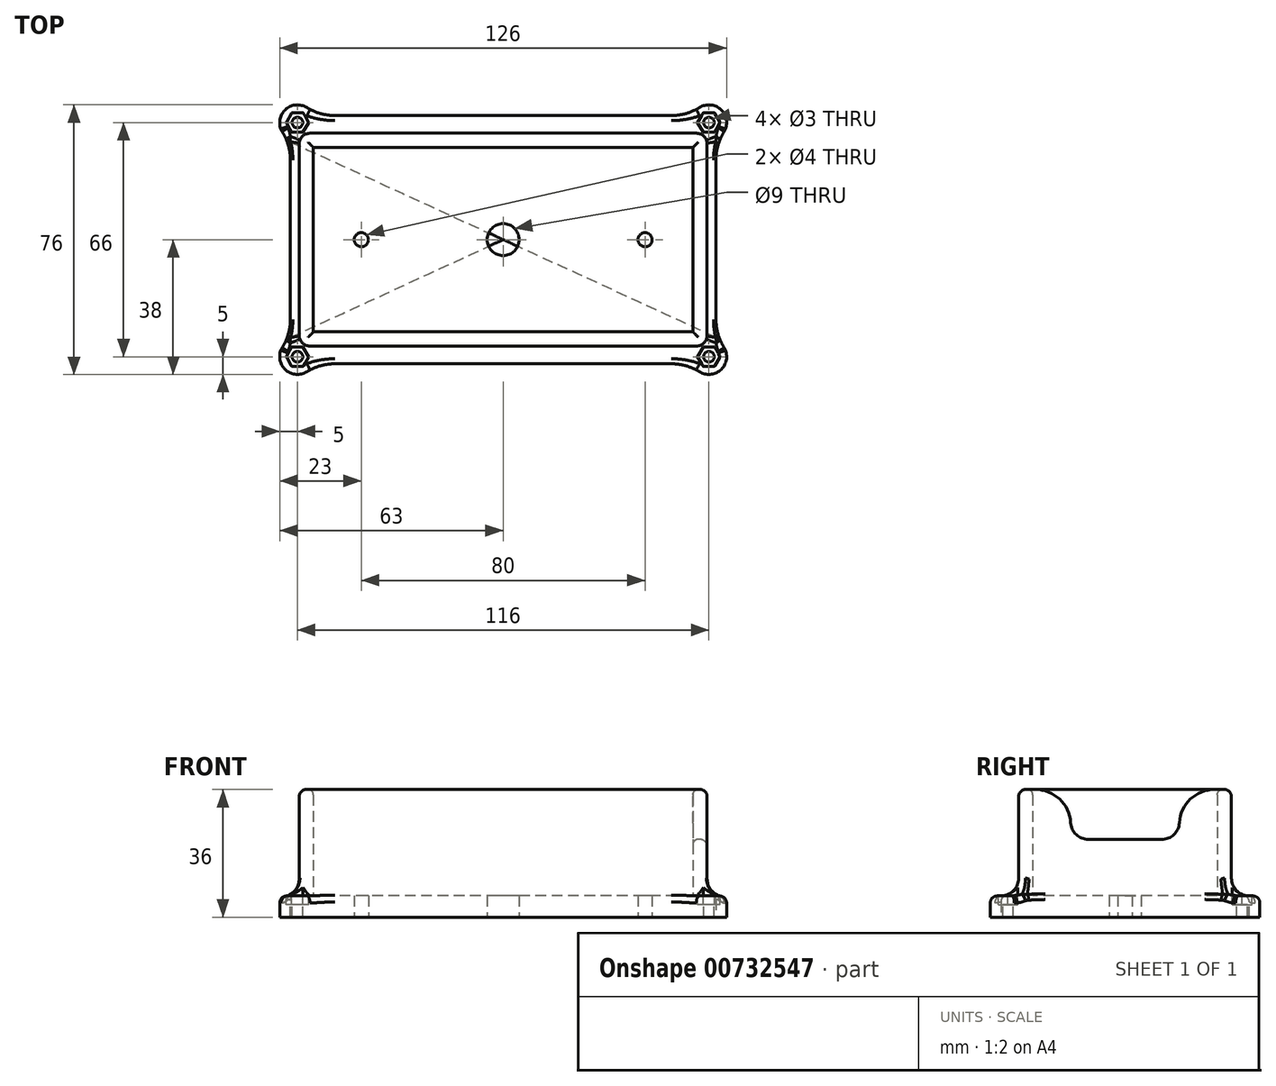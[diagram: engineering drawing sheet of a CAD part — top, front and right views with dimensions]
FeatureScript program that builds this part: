
annotation { "Feature Type Name" : "Feature", "Feature Type Description" : "" }
export const myFeature = defineFeature(function(context is Context, id is Id, definition is map)
    precondition{}
    {
        {
            var Q0;
            Q0=qCreatedBy(makeId("Top.planeOp"),FACE);
            var sketch = newSketch(context, id + "F0", { "sketchPlane" : qUnion([Q0])});
            skLineSegment(sketch, "E0.bottom", {"start": v(53.42, 35) * mm, "end": v(-53.42, 35) * mm});
            skLineSegment(sketch, "E0.top", {"start": v(53.42, -35) * mm, "end": v(-53.42, -35) * mm});
            skLineSegment(sketch, "E0.left", {"start": v(60, 28.42) * mm, "end": v(60, -28.42) * mm});
            skLineSegment(sketch, "E0.right", {"start": v(-60, 28.42) * mm, "end": v(-60, -28.42) * mm});
            skPoint(sketch, "E0.middle", {"position": v(0, 0) * mm});
            skLineSegment(sketch, "E1.bottom", {"start": v(58, -33) * mm, "end": v(-58, -33) * mm, "construction": true});
            skLineSegment(sketch, "E1.top", {"start": v(58, 33) * mm, "end": v(-58, 33) * mm, "construction": true});
            skLineSegment(sketch, "E1.left", {"start": v(58, 33) * mm, "end": v(58, -33) * mm, "construction": true});
            skLineSegment(sketch, "E1.right", {"start": v(-58, 33) * mm, "end": v(-58, -33) * mm, "construction": true});
            skArc(sketch, "E2", {"start": v(-53.42, 35) * mm, "mid": v(-61.54, 36.54) * mm, "end": v(-60, 28.42) * mm});
            skArc(sketch, "E3", {"start": v(-60, -28.42) * mm, "mid": v(-61.54, -36.54) * mm, "end": v(-53.42, -35) * mm});
            skArc(sketch, "E4", {"start": v(60, 28.42) * mm, "mid": v(61.54, 36.54) * mm, "end": v(53.42, 35) * mm});
            skArc(sketch, "E5", {"start": v(53.42, -35) * mm, "mid": v(61.54, -36.54) * mm, "end": v(60, -28.42) * mm});
            skPoint(sketch, "E6.orphan", {"position": v(-60, 35) * mm});
            skPoint(sketch, "E7.orphan", {"position": v(60, 35) * mm});
            skPoint(sketch, "E8.orphan", {"position": v(60, -35) * mm});
            skPoint(sketch, "E9.orphan", {"position": v(-60, -35) * mm});
            skSolve(sketch);
        }
        {
            var Q0;
            Q0=qSketchRegion(id+"F0",true);
            extrude(context, id + "F1", {"entities" : qUnion([Q0]), "depth" : 6 * mm, "offsetDistance" : 25 * mm});
        }
        {
            var Q0;
            Q0=makeQuery(id+"F1.opExtrude","SWEPT_EDGE",EDGE,{"disambiguationData":[OSD([sQuery(id+"F0.wireOp",EDGE,"E0.bottom"),sQuery(id+"F0.wireOp",EDGE,"E2")])]});
            var Q1;
            Q1=makeQuery(id+"F1.opExtrude","SWEPT_EDGE",EDGE,{"disambiguationData":[OSD([sQuery(id+"F0.wireOp",EDGE,"E0.bottom"),sQuery(id+"F0.wireOp",EDGE,"E4")])]});
            var Q2;
            Q2=makeQuery(id+"F1.opExtrude","SWEPT_EDGE",EDGE,{"disambiguationData":[OSD([sQuery(id+"F0.wireOp",EDGE,"E0.left"),sQuery(id+"F0.wireOp",EDGE,"E5")])]});
            var Q3;
            Q3=makeQuery(id+"F1.opExtrude","SWEPT_EDGE",EDGE,{"disambiguationData":[OSD([sQuery(id+"F0.wireOp",EDGE,"E0.left"),sQuery(id+"F0.wireOp",EDGE,"E4")])]});
            var Q4;
            Q4=makeQuery(id+"F1.opExtrude","SWEPT_EDGE",EDGE,{"disambiguationData":[OSD([sQuery(id+"F0.wireOp",EDGE,"E0.top"),sQuery(id+"F0.wireOp",EDGE,"E5")])]});
            var Q5;
            Q5=makeQuery(id+"F1.opExtrude","SWEPT_EDGE",EDGE,{"disambiguationData":[OSD([sQuery(id+"F0.wireOp",EDGE,"E0.top"),sQuery(id+"F0.wireOp",EDGE,"E3")])]});
            var Q6;
            Q6=makeQuery(id+"F1.opExtrude","SWEPT_EDGE",EDGE,{"disambiguationData":[OSD([sQuery(id+"F0.wireOp",EDGE,"E0.right"),sQuery(id+"F0.wireOp",EDGE,"E3")])]});
            var Q7;
            Q7=makeQuery(id+"F1.opExtrude","SWEPT_EDGE",EDGE,{"disambiguationData":[OSD([sQuery(id+"F0.wireOp",EDGE,"E0.right"),sQuery(id+"F0.wireOp",EDGE,"E2")])]});
            fillet(context, id + "F2", {"entities" : qUnion([Q0, Q1, Q2, Q3, Q4, Q5, Q6, Q7]), "radius" : 15 * mm, "tangentPropagation" : true, "allowEdgeOverflow" : false});
        }
        {
            var Q0;
            Q0=makeQuery(id+"F1.opExtrude","CAP_FACE",FACE,{"disambiguationData":[OSD([sQuery(id+"F0.wireOp",EDGE,"E0.bottom"),sQuery(id+"F0.wireOp",EDGE,"E0.top"),sQuery(id+"F0.wireOp",EDGE,"E0.left"),sQuery(id+"F0.wireOp",EDGE,"E0.right"),sQuery(id+"F0.wireOp",EDGE,"E2"),sQuery(id+"F0.wireOp",EDGE,"E3"),sQuery(id+"F0.wireOp",EDGE,"E4"),sQuery(id+"F0.wireOp",EDGE,"E5")])],"isStart":false});
            var sketch = newSketch(context, id + "F3", { "sketchPlane" : qUnion([Q0])});
            skLineSegment(sketch, "E10.bottom", {"start": v(57.5, 30) * mm, "end": v(-57.5, 30) * mm});
            skLineSegment(sketch, "E10.top", {"start": v(57.5, -30) * mm, "end": v(-57.5, -30) * mm});
            skLineSegment(sketch, "E10.left", {"start": v(57.5, 30) * mm, "end": v(57.5, -30) * mm});
            skLineSegment(sketch, "E10.right", {"start": v(-57.5, 30) * mm, "end": v(-57.5, -30) * mm});
            skPoint(sketch, "E10.middle", {"position": v(0, 0) * mm});
            skLineSegment(sketch, "E11.bottom", {"start": v(53.5, 26) * mm, "end": v(-53.5, 26) * mm});
            skLineSegment(sketch, "E11.top", {"start": v(53.5, -26) * mm, "end": v(-53.5, -26) * mm});
            skLineSegment(sketch, "E11.left", {"start": v(53.5, 26) * mm, "end": v(53.5, -26) * mm});
            skLineSegment(sketch, "E11.right", {"start": v(-53.5, 26) * mm, "end": v(-53.5, -26) * mm});
            skSolve(sketch);
        }
        {
            var Q0;
            Q0=qSketchRegion(id+"F3",true);
            extrude(context, id + "F4", {"entities" : qUnion([Q0]), "operationType" : NewBodyOperationType.ADD, "depth" : 30 * mm, "offsetDistance" : 25 * mm});
        }
        {
            var Q0;
            Q0=makeQuery(id+"F4.opExtrude","SWEPT_EDGE",EDGE,{"disambiguationData":[OSD([sQuery(id+"F3.wireOp",EDGE,"E10.top"),sQuery(id+"F3.wireOp",EDGE,"E10.right")])]});
            var Q1;
            Q1=makeQuery(id+"F4.opExtrude","SWEPT_EDGE",EDGE,{"disambiguationData":[OSD([sQuery(id+"F3.wireOp",EDGE,"E10.top"),sQuery(id+"F3.wireOp",EDGE,"E10.left")])]});
            var Q2;
            Q2=makeQuery(id+"F4.opExtrude","SWEPT_EDGE",EDGE,{"disambiguationData":[OSD([sQuery(id+"F3.wireOp",EDGE,"E10.bottom"),sQuery(id+"F3.wireOp",EDGE,"E10.left")])]});
            var Q3;
            Q3=makeQuery(id+"F4.opExtrude","SWEPT_EDGE",EDGE,{"disambiguationData":[OSD([sQuery(id+"F3.wireOp",EDGE,"E10.bottom"),sQuery(id+"F3.wireOp",EDGE,"E10.right")])]});
            fillet(context, id + "F5", {"entities" : qUnion([Q0, Q1, Q2, Q3]), "radius" : 3 * mm, "allowEdgeOverflow" : false});
        }
        {
            var Q0;
            Q0=makeQuery(id+"F4.opExtrude","CAP_EDGE",EDGE,{"disambiguationData":[OSD([sQuery(id+"F3.wireOp",EDGE,"E10.bottom")])],"isStart":true});
            fillet(context, id + "F6", {"entities" : qUnion([Q0]), "radius" : 5 * mm, "tangentPropagation" : true, "allowEdgeOverflow" : false});
        }
        {
            var Q0;
            Q0=makeQuery(id+"F6.opFillet","BLEND_EDGE",EDGE,{"blendedFrom":[makeQuery(id+"F4.opExtrude","CAP_EDGE",EDGE,{"disambiguationData":[OSD([sQuery(id+"F3.wireOp",EDGE,"E10.bottom")])],"isStart":true}),makeQuery(id+"F1.opExtrude","SWEPT_FACE",FACE,{"disambiguationData":[OSD([sQuery(id+"F0.wireOp",EDGE,"E0.bottom")])]})],"blendedInto":[makeQuery(id+"F1.opExtrude","SWEPT_FACE",FACE,{"disambiguationData":[OSD([sQuery(id+"F0.wireOp",EDGE,"E0.bottom")])]})]});
            fillet(context, id + "F7", {"entities" : qUnion([Q0]), "radius" : 2 * mm, "tangentPropagation" : true, "allowEdgeOverflow" : false});
        }
        {
            var Q0;
            Q0=makeQuery(id+"F4.opExtrude","SWEPT_FACE",FACE,{"disambiguationData":[OSD([sQuery(id+"F3.wireOp",EDGE,"E10.left")])]});
            var sketch = newSketch(context, id + "F8", { "sketchPlane" : qUnion([Q0])});
            skLineSegment(sketch, "E12.bottom", {"start": v(15.3, 21.93) * mm, "end": v(-15.3, 21.93) * mm});
            skLineSegment(sketch, "E12.top", {"start": v(15.3, 50.07) * mm, "end": v(-15.3, 50.07) * mm});
            skLineSegment(sketch, "E12.left", {"start": v(15.3, 21.93) * mm, "end": v(15.3, 50.07) * mm});
            skLineSegment(sketch, "E12.right", {"start": v(-15.3, 21.93) * mm, "end": v(-15.3, 50.07) * mm});
            skPoint(sketch, "E12.middle", {"position": v(0, 36) * mm});
            skSolve(sketch);
        }
        {
            var Q0;
            Q0 = qSketchRegion(id + "F8", true);
            extrude(context, id + "F9", {"entities" : qUnion([Q0]), "operationType" : NewBodyOperationType.REMOVE, "oppositeDirection" : true, "depth" : 25 * mm, "offsetDistance" : 25 * mm});
        }
        {
            var Q0;
            Q0=makeQuery(id+"F9.boolean.opBoolean","INTERSECT",EDGE,{"derivedFrom":[makeQuery(id+"F4.opExtrude","CAP_FACE",FACE,{"disambiguationData":[OSD([sQuery(id+"F3.wireOp",EDGE,"E10.bottom"),sQuery(id+"F3.wireOp",EDGE,"E10.top"),sQuery(id+"F3.wireOp",EDGE,"E10.left"),sQuery(id+"F3.wireOp",EDGE,"E10.right"),sQuery(id+"F3.wireOp",EDGE,"E11.bottom"),sQuery(id+"F3.wireOp",EDGE,"E11.top"),sQuery(id+"F3.wireOp",EDGE,"E11.left"),sQuery(id+"F3.wireOp",EDGE,"E11.right")])],"isStart":false}),makeQuery(id+"F9.opExtrude","SWEPT_FACE",FACE,{"disambiguationData":[OSD([sQuery(id+"F8.wireOp",EDGE,"E12.left")])]})]});
            var Q1;
            Q1=makeQuery(id+"F9.boolean.opBoolean","INTERSECT",EDGE,{"derivedFrom":[makeQuery(id+"F4.opExtrude","CAP_FACE",FACE,{"disambiguationData":[OSD([sQuery(id+"F3.wireOp",EDGE,"E10.bottom"),sQuery(id+"F3.wireOp",EDGE,"E10.top"),sQuery(id+"F3.wireOp",EDGE,"E10.left"),sQuery(id+"F3.wireOp",EDGE,"E10.right"),sQuery(id+"F3.wireOp",EDGE,"E11.bottom"),sQuery(id+"F3.wireOp",EDGE,"E11.top"),sQuery(id+"F3.wireOp",EDGE,"E11.left"),sQuery(id+"F3.wireOp",EDGE,"E11.right")])],"isStart":false}),makeQuery(id+"F9.opExtrude","SWEPT_FACE",FACE,{"disambiguationData":[OSD([sQuery(id+"F8.wireOp",EDGE,"E12.right")])]})]});
            fillet(context, id + "F10", {"entities" : qUnion([Q0, Q1]), "radius" : 10 * mm, "tangentPropagation" : true, "allowEdgeOverflow" : false});
        }
        {
            var Q0;
            Q0=makeQuery(id+"F9.boolean.opBoolean","COPY",EDGE,{"derivedFrom":makeQuery(id+"F9.opExtrude","SWEPT_EDGE",EDGE,{"disambiguationData":[OSD([sQuery(id+"F8.wireOp",EDGE,"E12.bottom"),sQuery(id+"F8.wireOp",EDGE,"E12.left")])]})});
            var Q1;
            Q1=makeQuery(id+"F9.boolean.opBoolean","COPY",EDGE,{"derivedFrom":makeQuery(id+"F9.opExtrude","SWEPT_EDGE",EDGE,{"disambiguationData":[OSD([sQuery(id+"F8.wireOp",EDGE,"E12.bottom"),sQuery(id+"F8.wireOp",EDGE,"E12.right")])]})});
            fillet(context, id + "F11", {"entities" : qUnion([Q0, Q1]), "radius" : 5 * mm, "tangentPropagation" : true, "allowEdgeOverflow" : false});
        }
        {
            var Q0;
            Q0=makeQuery(id+"FcA09zrrW4XeXJK_1.boolean.opBoolean","COPY",EDGE,{"derivedFrom":makeQuery(id+"FcA09zrrW4XeXJK_1.opExtrude","CAP_EDGE",EDGE,{"disambiguationData":[OSD([sQuery(id+"Fv4TZC5OFzZsvTr_1.wireOp",EDGE,"FDxE1tWj-xLRE-T8vv-3hwI-uIhzQXojzkdN")])],"isStart":true})});
            var Q1;
            Q1=makeQuery(id+"F4.opExtrude","CAP_EDGE",EDGE,{"disambiguationData":[OSD([sQuery(id+"F3.wireOp",EDGE,"E10.top")])],"isStart":false});
            fillet(context, id + "F12", {"entities" : qUnion([Q0, Q1]), "radius" : 2 * mm, "tangentPropagation" : true, "allowEdgeOverflow" : false});
        }
        {
            var Q0;
            Q0=makeQuery(id+"F4.opExtrude","CAP_EDGE",EDGE,{"disambiguationData":[OSD([sQuery(id+"F3.wireOp",EDGE,"E11.right")])],"isStart":false});
            var Q1;
            Q1=makeQuery(id+"F4.opExtrude","CAP_EDGE",EDGE,{"disambiguationData":[OSD([sQuery(id+"F3.wireOp",EDGE,"E11.bottom")])],"isStart":false});
            var Q2;
            Q2=makeQuery(id+"F4.opExtrude","CAP_EDGE",EDGE,{"disambiguationData":[OSD([sQuery(id+"F3.wireOp",EDGE,"E11.left")])],"isStart":false});
            var Q3;
            Q3=makeQuery(id+"F4.opExtrude","CAP_EDGE",EDGE,{"disambiguationData":[OSD([sQuery(id+"F3.wireOp",EDGE,"E11.top")])],"isStart":false});
            fillet(context, id + "F13", {"entities" : qUnion([Q0, Q1, Q2, Q3]), "radius" : 1.5 * mm, "tangentPropagation" : true, "allowEdgeOverflow" : false});
        }
        {
            var Q0;
            Q0=makeQuery(id+"F4.boolean.opBoolean","SPLIT",FACE,{"disambiguationData":[TD([makeQuery(id+"F4.opExtrude","SWEPT_FACE",FACE,{"disambiguationData":[OSD([sQuery(id+"F3.wireOp",EDGE,"E11.bottom")])]})])],"derivedFrom":makeQuery(id+"F1.opExtrude","CAP_FACE",FACE,{"disambiguationData":[OSD([sQuery(id+"F0.wireOp",EDGE,"E0.bottom"),sQuery(id+"F0.wireOp",EDGE,"E0.top"),sQuery(id+"F0.wireOp",EDGE,"E0.left"),sQuery(id+"F0.wireOp",EDGE,"E0.right"),sQuery(id+"F0.wireOp",EDGE,"E2"),sQuery(id+"F0.wireOp",EDGE,"E3"),sQuery(id+"F0.wireOp",EDGE,"E4"),sQuery(id+"F0.wireOp",EDGE,"E5")])],"isStart":false})});
            var sketch = newSketch(context, id + "F14", { "sketchPlane" : qUnion([Q0])});
            skLineSegment(sketch, "E13.bottom", {"start": v(58, 33) * mm, "end": v(-58, 33) * mm, "construction": true});
            skLineSegment(sketch, "E13.top", {"start": v(58, -33) * mm, "end": v(-58, -33) * mm, "construction": true});
            skLineSegment(sketch, "E13.left", {"start": v(58, 33) * mm, "end": v(58, -33) * mm, "construction": true});
            skLineSegment(sketch, "E13.right", {"start": v(-58, 33) * mm, "end": v(-58, -33) * mm, "construction": true});
            skPoint(sketch, "E13.middle", {"position": v(0, 0) * mm});
            skCircle(sketch, "E14.cCircle", {"center": v(-58, 33) * mm, "radius": 2.75 * mm, "construction": true});
            skLineSegment(sketch, "E14.0", {"start": v(-56.41, 30.25) * mm, "end": v(-59.59, 30.25) * mm});
            skLineSegment(sketch, "E14.1", {"start": v(-59.59, 30.25) * mm, "end": v(-61.18, 33) * mm});
            skLineSegment(sketch, "E14.2", {"start": v(-61.18, 33) * mm, "end": v(-59.59, 35.75) * mm});
            skLineSegment(sketch, "E14.3", {"start": v(-59.59, 35.75) * mm, "end": v(-56.41, 35.75) * mm});
            skLineSegment(sketch, "E14.4", {"start": v(-56.41, 35.75) * mm, "end": v(-54.82, 33) * mm});
            skLineSegment(sketch, "E14.5", {"start": v(-54.82, 33) * mm, "end": v(-56.41, 30.25) * mm});
            skPoint(sketch, "E14.0.midPoint", {"position": v(-58, 30.25) * mm});
            skCircle(sketch, "E15.cCircle", {"center": v(58, 33) * mm, "radius": 2.75 * mm, "construction": true});
            skLineSegment(sketch, "E15.0", {"start": v(54.82, 33) * mm, "end": v(56.41, 35.75) * mm});
            skLineSegment(sketch, "E15.1", {"start": v(56.41, 35.75) * mm, "end": v(59.59, 35.75) * mm});
            skLineSegment(sketch, "E15.2", {"start": v(59.59, 35.75) * mm, "end": v(61.18, 33) * mm});
            skLineSegment(sketch, "E15.3", {"start": v(61.18, 33) * mm, "end": v(59.59, 30.25) * mm});
            skLineSegment(sketch, "E15.4", {"start": v(59.59, 30.25) * mm, "end": v(56.41, 30.25) * mm});
            skLineSegment(sketch, "E15.5", {"start": v(56.41, 30.25) * mm, "end": v(54.82, 33) * mm});
            skPoint(sketch, "E15.0.midPoint", {"position": v(55.62, 34.38) * mm});
            skCircle(sketch, "E16.cCircle", {"center": v(58, -33) * mm, "radius": 2.75 * mm, "construction": true});
            skPoint(sketch, "E16.cCircle.perimeterSnap0", {"position": v(55.62, 31.62) * mm});
            skLineSegment(sketch, "E16.0", {"start": v(56.41, -35.75) * mm, "end": v(54.82, -33) * mm});
            skLineSegment(sketch, "E16.1", {"start": v(54.82, -33) * mm, "end": v(56.41, -30.25) * mm});
            skLineSegment(sketch, "E16.2", {"start": v(56.41, -30.25) * mm, "end": v(59.59, -30.25) * mm});
            skLineSegment(sketch, "E16.3", {"start": v(59.59, -30.25) * mm, "end": v(61.18, -33) * mm});
            skLineSegment(sketch, "E16.4", {"start": v(61.18, -33) * mm, "end": v(59.59, -35.75) * mm});
            skLineSegment(sketch, "E16.5", {"start": v(59.59, -35.75) * mm, "end": v(56.41, -35.75) * mm});
            skPoint(sketch, "E16.0.midPoint", {"position": v(55.62, -34.38) * mm});
            skPoint(sketch, "E16.0.midPoint.positionSnap0", {"position": v(55.62, 31.63) * mm});
            skCircle(sketch, "E17.cCircle", {"center": v(-58, -33) * mm, "radius": 2.75 * mm, "construction": true});
            skLineSegment(sketch, "E17.0", {"start": v(-59.59, -35.75) * mm, "end": v(-61.18, -33) * mm});
            skLineSegment(sketch, "E17.1", {"start": v(-61.18, -33) * mm, "end": v(-59.59, -30.25) * mm});
            skLineSegment(sketch, "E17.2", {"start": v(-59.59, -30.25) * mm, "end": v(-56.41, -30.25) * mm});
            skLineSegment(sketch, "E17.3", {"start": v(-56.41, -30.25) * mm, "end": v(-54.82, -33) * mm});
            skLineSegment(sketch, "E17.4", {"start": v(-54.82, -33) * mm, "end": v(-56.41, -35.75) * mm});
            skLineSegment(sketch, "E17.5", {"start": v(-56.41, -35.75) * mm, "end": v(-59.59, -35.75) * mm});
            skPoint(sketch, "E17.0.midPoint", {"position": v(-60.38, -34.37) * mm});
            skSolve(sketch);
        }
        {
            var Q0;
            Q0=qSketchRegion(id+"F14",true);
            extrude(context, id + "F15", {"entities" : qUnion([Q0]), "operationType" : NewBodyOperationType.REMOVE, "oppositeDirection" : true, "depth" : 2.5 * mm, "offsetDistance" : 25 * mm, "hasSecondDirection" : true, "secondDirectionOppositeDirection" : false, "secondDirectionDepth" : 15 * mm});
        }
        {
            var Q0;
            Q0=makeQuery(id+"F4.boolean.opBoolean","SPLIT",FACE,{"disambiguationData":[TD([makeQuery(id+"F4.opExtrude","SWEPT_FACE",FACE,{"disambiguationData":[OSD([sQuery(id+"F3.wireOp",EDGE,"E11.bottom")])]})])],"derivedFrom":makeQuery(id+"F1.opExtrude","CAP_FACE",FACE,{"disambiguationData":[OSD([sQuery(id+"F0.wireOp",EDGE,"E0.bottom"),sQuery(id+"F0.wireOp",EDGE,"E0.top"),sQuery(id+"F0.wireOp",EDGE,"E0.left"),sQuery(id+"F0.wireOp",EDGE,"E0.right"),sQuery(id+"F0.wireOp",EDGE,"E2"),sQuery(id+"F0.wireOp",EDGE,"E3"),sQuery(id+"F0.wireOp",EDGE,"E4"),sQuery(id+"F0.wireOp",EDGE,"E5")])],"isStart":false})});
            var sketch = newSketch(context, id + "F16", { "sketchPlane" : qUnion([Q0])});
            skLineSegment(sketch, "E18.bottom", {"start": v(-58, 33) * mm, "end": v(58, 33) * mm, "construction": true});
            skLineSegment(sketch, "E18.top", {"start": v(-58, -33) * mm, "end": v(58, -33) * mm, "construction": true});
            skLineSegment(sketch, "E18.left", {"start": v(-58, 33) * mm, "end": v(-58, -33) * mm, "construction": true});
            skLineSegment(sketch, "E18.right", {"start": v(58, 33) * mm, "end": v(58, -33) * mm, "construction": true});
            skPoint(sketch, "E18.middle", {"position": v(0, 0) * mm});
            skCircle(sketch, "E19", {"center": v(-58, 33) * mm, "radius": 1.5 * mm});
            skCircle(sketch, "E20", {"center": v(-58, -33) * mm, "radius": 1.5 * mm});
            skCircle(sketch, "E21", {"center": v(58, 33) * mm, "radius": 1.5 * mm});
            skCircle(sketch, "E22", {"center": v(58, -33) * mm, "radius": 1.5 * mm});
            skSolve(sketch);
        }
        {
            var Q0;
            Q0=qSketchRegion(id+"F16",true);
            extrude(context, id + "F17", {"entities" : qUnion([Q0]), "operationType" : NewBodyOperationType.REMOVE, "oppositeDirection" : true, "depth" : 25 * mm, "offsetDistance" : 25 * mm});
        }
        {
            var Q0;
            Q0=makeQuery(id+"F1.opExtrude","CAP_FACE",FACE,{"disambiguationData":[OSD([sQuery(id+"F0.wireOp",EDGE,"E0.bottom"),sQuery(id+"F0.wireOp",EDGE,"E0.top"),sQuery(id+"F0.wireOp",EDGE,"E0.left"),sQuery(id+"F0.wireOp",EDGE,"E0.right"),sQuery(id+"F0.wireOp",EDGE,"E2"),sQuery(id+"F0.wireOp",EDGE,"E3"),sQuery(id+"F0.wireOp",EDGE,"E4"),sQuery(id+"F0.wireOp",EDGE,"E5")])],"isStart":true});
            var sketch = newSketch(context, id + "F18", { "sketchPlane" : qUnion([Q0])});
            skLineSegment(sketch, "E23", {"start": v(-72.3, 0) * mm, "end": v(71.2, 0) * mm, "construction": true});
            skCircle(sketch, "E24", {"center": v(0, 0) * mm, "radius": 4.5 * mm});
            skCircle(sketch, "E25", {"center": v(40, 0) * mm, "radius": 2 * mm});
            skCircle(sketch, "E26", {"center": v(-40, 0) * mm, "radius": 2 * mm});
            skSolve(sketch);
        }
        {
            var Q0;
            Q0 = qSketchRegion(id + "F18", true);
            extrude(context, id + "F19", {"entities" : qUnion([Q0]), "operationType" : NewBodyOperationType.REMOVE, "oppositeDirection" : true, "depth" : 25 * mm, "offsetDistance" : 25 * mm});
        }
    });
